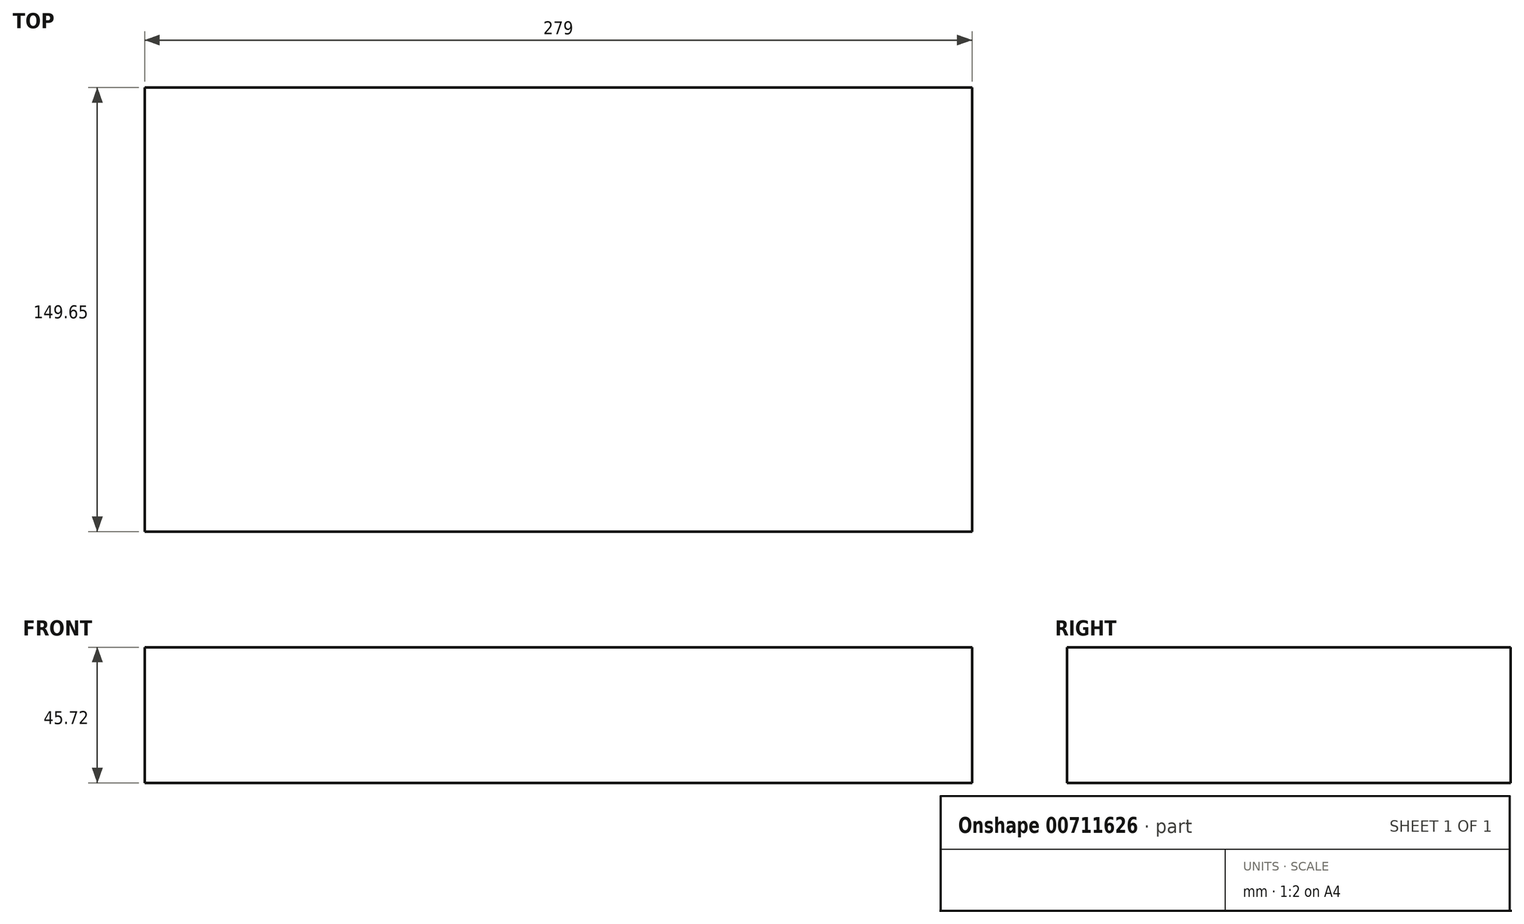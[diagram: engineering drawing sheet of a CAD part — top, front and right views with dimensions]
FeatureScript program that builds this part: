
annotation { "Feature Type Name" : "Feature", "Feature Type Description" : "" }
export const myFeature = defineFeature(function(context is Context, id is Id, definition is map)
    precondition{}
    {
        {
            var Q0;
            Q0=qCreatedBy(makeId("Top.planeOp"),FACE);
            var sketch = newSketch(context, id + "F0", { "sketchPlane" : qUnion([Q0])});
            skLineSegment(sketch, "E0.bottom", {"start": v(-140.47, 73.05) * mm, "end": v(138.53, 73.05) * mm});
            skLineSegment(sketch, "E0.top", {"start": v(-140.47, -76.6) * mm, "end": v(138.53, -76.6) * mm});
            skLineSegment(sketch, "E0.left", {"start": v(-140.47, 73.05) * mm, "end": v(-140.47, -76.6) * mm});
            skLineSegment(sketch, "E0.right", {"start": v(138.53, 73.05) * mm, "end": v(138.53, -76.6) * mm});
            skSolve(sketch);
        }
        {
            var Q0;
            Q0=makeQuery(id+"F0.imprint","IMPRINT",FACE,{"disambiguationData":[TD([[makeQuery(id+"F0.imprint","IMPRINT",EDGE,{"derivedFrom":sQuery(id+"F0.wireOp",EDGE,"E0.bottom")}),-1.0]])]});
            extrude(context, id + "F1", {"entities" : qUnion([Q0]), "depth" : 45.72 * mm, "offsetDistance" : 25.4 * mm});
        }
    });
